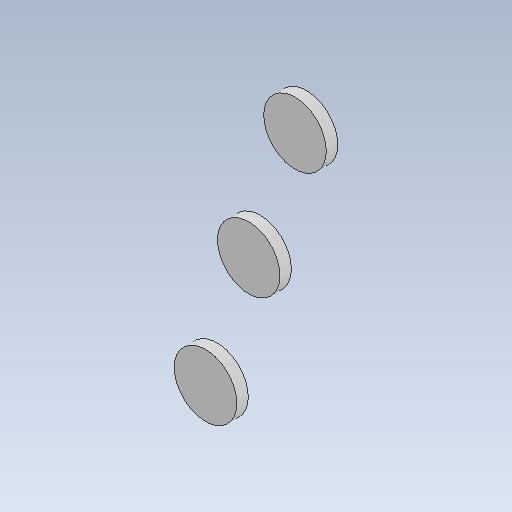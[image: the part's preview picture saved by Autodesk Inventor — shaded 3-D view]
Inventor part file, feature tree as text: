
AUTODESK INVENTOR PART (.ipt)
format: ipt  version: 2020 (Build 240168000, 168)  size: 84,992 bytes
history: native  units: in
note: dims shown in document units (in); Inventor stores cm internally (conversion verified against a paired STEP export)
features: other x3, sketch x1, plane x1
ambient origin geometry x8: Origin, YZ Plane, XZ Plane, XY Plane, X Axis, Y Axis, Z Axis, Center Point
bodies: Solid1 (feature_tree)
feature tree (5):
  other  "WheelCover.ipt"
  other  "Solid1::WheelCover.ipt"
  other  "TaggingFeature1"
  sketch  "Sketch1"  dims[d0=0.3937in]
  plane  "Work Plane1"
